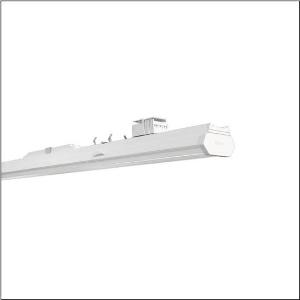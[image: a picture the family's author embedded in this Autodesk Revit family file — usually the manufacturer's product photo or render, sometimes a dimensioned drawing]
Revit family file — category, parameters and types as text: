
# Revit family: licross_r__11_protected_mo_51td1bcn485g_09c4
name_source: partatom
category: Lighting Fixtures
units: mm (PartAtom-declared; Revit-internal decimal feet)

## family parameters
Cut with Voids When Loaded = No
Host = Face
Light Source = No
Part Type = Normal
Room Calculation Point = No
Round Connector Dimension = Use Diameter
Shared = No

## types (1)
- --- (1 x LED, 8520 lm, 49.4 W, 4000K)
    Apparent Load = 49 VA
    CIE Flux Codes = 54 82 95 97 100
    Color Rendering = 80
    Color Temperature = 4000K
    Default Elevation = 1800 mm
    Description = Licross® 11 Protected MO, luminaire insert, of sheet steel, galvanised, coil coated, white, length: 1.500mm, width: 90mm, height: 101mm, LED rated luminous flux: 8.520lm, light colour: 840, control gear: ON/OFF Multilumen, CLOi, with plug, 3-pole, with phase selection, mains connection: 220..240V, AC, 50/60Hz, start of lifetime: 49W, end of service life: 55W, halogen-free wiring, primary optical cover: cover, of PMMA, light emission: direct distribution, primary light characteristic: symmetric, protection rating (complete): IP54, insulation class (complete): insulation class I (protective earthing), certification: CE, ENEC, VDE, UKCA, protection symbol: D if used in an environment with non-conductive dust loads with corresponding accessories, impact resistance: IK06, permissible ambient temperature for indoor applications: -35..+40°C, corresponds to IFS (International Featured Standards) requirements for safety and quality in the food industry, reducing of maximum allowable ambient temperature of 5°C with ceiling mounting, LABS conformity tested according to VDMA 24364:2018-05, packaging unit: 1 piece
    Height = 92 mm
    Lamp = 1 x LED
    Lamp Light Flux = 8520 lm
    Lamp Power = 49.4 W
    Lamp count = 1
    Length = 1500 mm
    Luminous efficacy = 172 lm/W
    Manufacturer = Siteco
    ModVariant = No
    Model = 51TD1BCN485G
    Mounting Place = Ceiling
    Mounting Type = Pendant
    Number of Poles = 1
    OnlyDefault = Yes
    Power Factor = 1
    Product Name = Licross® 11 Protected MO
    Product group = luminaire insert
    ProductGroupID = 901
    Protection Class = Protection class I
    Protection Degree = IP 54
    RLX_Detail_Level = 1
    RLX_Emergency_Light_Flux = 0 lm
    RLX_Emergency_Type = 0
    RLX_Emergency_Type_DB = No
    RlxData = <blob elided: 22113 chars, md5=85c050e8>
    Socket = socket
    Standby Power = 0 W
    System Light Flux = 8520 lm
    System Power = 49 W
    Type Comments = factory setting: luminous flux: 100 % | (A | C | E) | 113 mA
    Type Image = l_1256145.jpg
    URL = http://relux.com
    VarID = @adj_055367
    Voltage = 0 V
    Weight = 0.00 kg
    Width = 88 mm

## geometry (parser evidence)
native form markers: Blend x4, Sweep x13
no freeform markers — native parametric forms only
